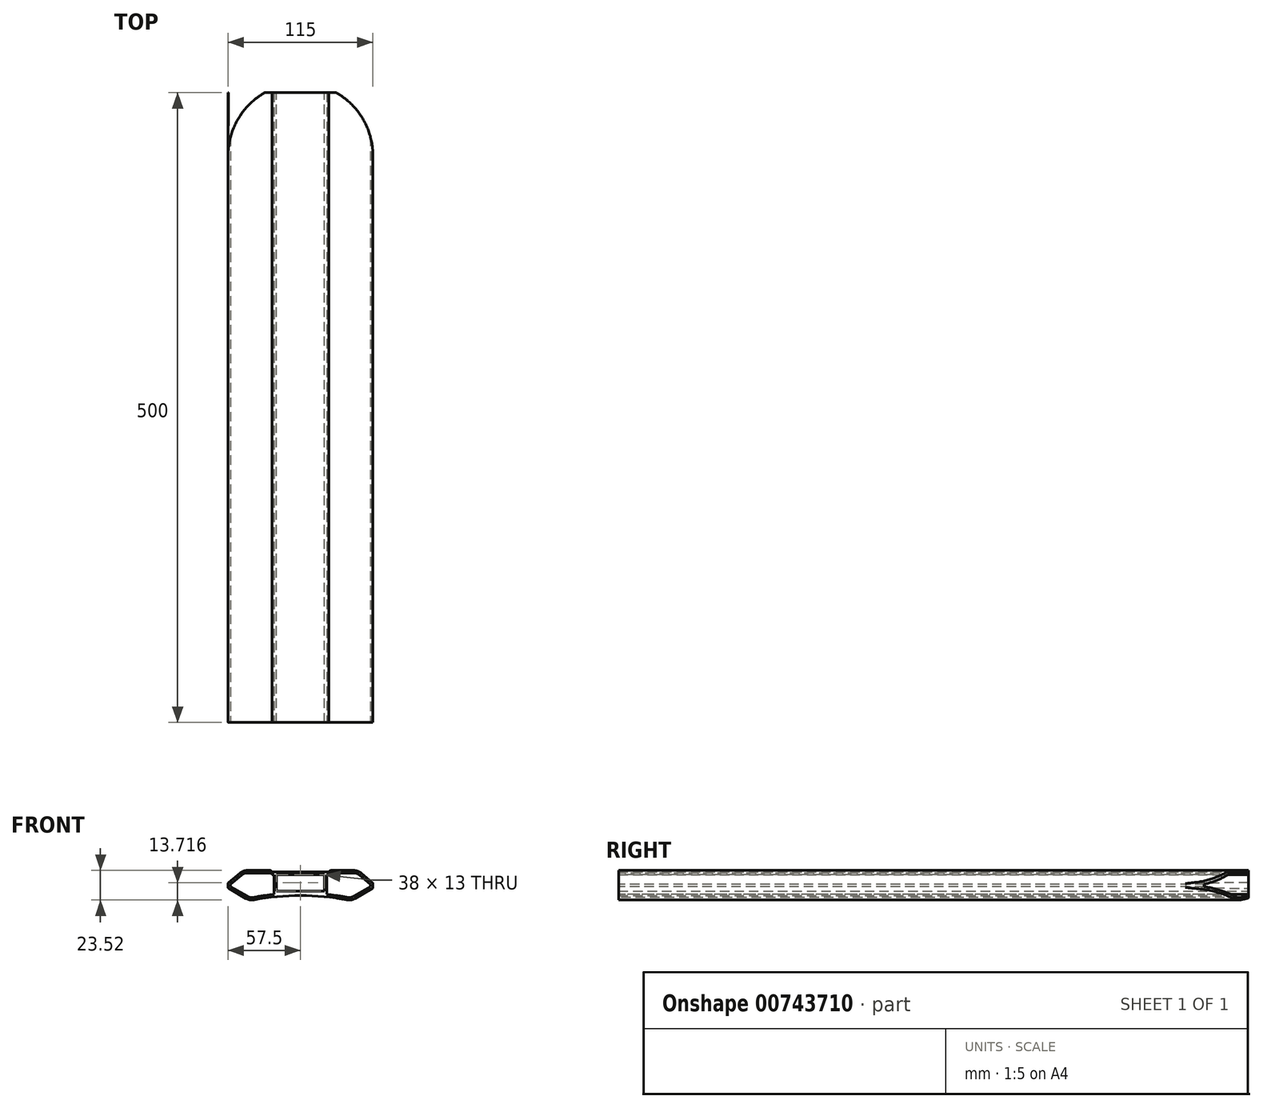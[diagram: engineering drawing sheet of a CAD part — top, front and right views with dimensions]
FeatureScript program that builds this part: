
annotation { "Feature Type Name" : "Feature", "Feature Type Description" : "" }
export const myFeature = defineFeature(function(context is Context, id is Id, definition is map)
    precondition{}
    {
        {
            var Q0;
            Q0=qCreatedBy(makeId("Front.planeOp"),FACE);
            var sketch = newSketch(context, id + "F0", { "sketchPlane" : qUnion([Q0])});
            skLineSegment(sketch, "E0", {"start": v(0, 0) * mm, "end": v(0, 25) * mm, "construction": true});
            skLineSegment(sketch, "E1", {"start": v(0, 5.38) * mm, "end": v(22.5, 5.38) * mm});
            skLineSegment(sketch, "E2", {"start": v(22.5, 5.38) * mm, "end": v(22.5, 6.68) * mm});
            skLineSegment(sketch, "E3", {"start": v(22.5, 6.68) * mm, "end": v(45.58, 6.68) * mm});
            skLineSegment(sketch, "E4", {"start": v(45.58, 6.68) * mm, "end": v(57.5, -3.32) * mm});
            skLineSegment(sketch, "E5", {"start": v(57.5, -3.32) * mm, "end": v(57.5, -7.32) * mm});
            skLineSegment(sketch, "E6", {"start": v(57.5, -7.32) * mm, "end": v(40.18, -17.32) * mm});
            skLineSegment(sketch, "E7.MirrorCS", {"start": v(-45.58, 6.68) * mm, "end": v(-57.5, -3.32) * mm});
            skLineSegment(sketch, "E8.MirrorCS", {"start": v(-22.5, 5.38) * mm, "end": v(-22.5, 6.68) * mm});
            skLineSegment(sketch, "E9.MirrorCS", {"start": v(-57.5, -3.32) * mm, "end": v(-57.5, -7.32) * mm});
            skLineSegment(sketch, "E10.MirrorCS", {"start": v(-22.5, 6.68) * mm, "end": v(-45.58, 6.68) * mm});
            skLineSegment(sketch, "E11.MirrorCS", {"start": v(0, 5.38) * mm, "end": v(-22.5, 5.38) * mm});
            skLineSegment(sketch, "E12.MirrorCS", {"start": v(-57.5, -7.32) * mm, "end": v(-40.18, -17.32) * mm});
            skArc(sketch, "E13", {"start": v(40.18, -17.32) * mm, "mid": v(0, -13.25) * mm, "end": v(-40.18, -17.32) * mm});
            skSolve(sketch);
        }
        {
            var Q0;
            Q0=makeQuery(id+"F0.imprint","IMPRINT",FACE,{"disambiguationData":[TD([[makeQuery(id+"F0.imprint","IMPRINT",EDGE,{"derivedFrom":sQuery(id+"F0.wireOp",EDGE,"E1")}),-1.0]])]});
            var sketch = newSketch(context, id + "F1", { "sketchPlane" : qUnion([Q0])});
            skLineSegment(sketch, "E14.bottom", {"start": v(-19, 3.38) * mm, "end": v(19, 3.38) * mm});
            skLineSegment(sketch, "E14.top", {"start": v(-19, -9.62) * mm, "end": v(19, -9.62) * mm});
            skLineSegment(sketch, "E14.left", {"start": v(-19, 3.38) * mm, "end": v(-19, -9.62) * mm});
            skLineSegment(sketch, "E14.right", {"start": v(19, 3.38) * mm, "end": v(19, -9.62) * mm});
            skLineSegment(sketch, "E15", {"start": v(0, 0) * mm, "end": v(0, -33.5) * mm, "construction": true});
            skSolve(sketch);
        }
        {
            var Q0;
            Q0=makeQuery(id+"F0.imprint","IMPRINT",FACE,{"disambiguationData":[TD([[makeQuery(id+"F0.imprint","IMPRINT",EDGE,{"derivedFrom":sQuery(id+"F0.wireOp",EDGE,"E1")}),-1.0]])]});
            extrude(context, id + "F2", {"entities" : qUnion([Q0]), "depth" : 500 * mm, "offsetDistance" : 25 * mm});
        }
        {
            var Q0;
            Q0=makeQuery(id+"F1.imprint","IMPRINT",FACE,{"disambiguationData":[TD([[makeQuery(id+"F1.imprint","IMPRINT",EDGE,{"derivedFrom":sQuery(id+"F1.wireOp",EDGE,"E14.bottom")}),-1.0]])]});
            extrude(context, id + "F3", {"entities" : qUnion([Q0]), "operationType" : NewBodyOperationType.REMOVE, "depth" : 600 * mm, "offsetDistance" : 25 * mm});
        }
        {
            var Q0;
            Q0=makeQuery(id+"F2.opExtrude","SWEPT_EDGE",EDGE,{"disambiguationData":[OSD([sQuery(id+"F0.wireOp",EDGE,"E8.MirrorCS"),sQuery(id+"F0.wireOp",EDGE,"E10.MirrorCS")])]});
            var Q1;
            Q1=makeQuery(id+"F2.opExtrude","SWEPT_EDGE",EDGE,{"disambiguationData":[OSD([sQuery(id+"F0.wireOp",EDGE,"E2"),sQuery(id+"F0.wireOp",EDGE,"E3")])]});
            fillet(context, id + "F4", {"entities" : qUnion([Q0, Q1]), "radius" : 2 * mm, "tangentPropagation" : true, "allowEdgeOverflow" : false});
        }
        {
            var Q0;
            Q0=makeQuery(id+"F2.opExtrude","SWEPT_EDGE",EDGE,{"disambiguationData":[OSD([sQuery(id+"F0.wireOp",EDGE,"E7.MirrorCS"),sQuery(id+"F0.wireOp",EDGE,"E10.MirrorCS")])]});
            var Q1;
            Q1=makeQuery(id+"F2.opExtrude","SWEPT_EDGE",EDGE,{"disambiguationData":[OSD([sQuery(id+"F0.wireOp",EDGE,"E12.MirrorCS"),sQuery(id+"F0.wireOp",EDGE,"E13")])]});
            var Q2;
            Q2=makeQuery(id+"F2.opExtrude","SWEPT_EDGE",EDGE,{"disambiguationData":[OSD([sQuery(id+"F0.wireOp",EDGE,"E6"),sQuery(id+"F0.wireOp",EDGE,"E13")])]});
            var Q3;
            Q3=makeQuery(id+"F2.opExtrude","SWEPT_EDGE",EDGE,{"disambiguationData":[OSD([sQuery(id+"F0.wireOp",EDGE,"E3"),sQuery(id+"F0.wireOp",EDGE,"E4")])]});
            fillet(context, id + "F5", {"entities" : qUnion([Q0, Q1, Q2, Q3]), "radius" : 9 * mm, "tangentPropagation" : true, "allowEdgeOverflow" : false});
        }
        {
            var Q0;
            Q0=makeQuery(id+"F2.opExtrude","SWEPT_EDGE",EDGE,{"disambiguationData":[OSD([sQuery(id+"F0.wireOp",EDGE,"E4"),sQuery(id+"F0.wireOp",EDGE,"E5")])]});
            var Q1;
            Q1=makeQuery(id+"F2.opExtrude","SWEPT_EDGE",EDGE,{"disambiguationData":[OSD([sQuery(id+"F0.wireOp",EDGE,"E5"),sQuery(id+"F0.wireOp",EDGE,"E6")])]});
            var Q2;
            Q2=makeQuery(id+"F2.opExtrude","SWEPT_EDGE",EDGE,{"disambiguationData":[OSD([sQuery(id+"F0.wireOp",EDGE,"E9.MirrorCS"),sQuery(id+"F0.wireOp",EDGE,"E12.MirrorCS")])]});
            var Q3;
            Q3=makeQuery(id+"F2.opExtrude","SWEPT_EDGE",EDGE,{"disambiguationData":[OSD([sQuery(id+"F0.wireOp",EDGE,"E7.MirrorCS"),sQuery(id+"F0.wireOp",EDGE,"E9.MirrorCS")])]});
            fillet(context, id + "F6", {"entities" : qUnion([Q0, Q1, Q2, Q3]), "radius" : 1 * mm, "tangentPropagation" : true, "allowEdgeOverflow" : false});
        }
        {
            var Q0;
            Q0=makeQuery(id+"F2.opExtrude","CAP_FACE",FACE,{"disambiguationData":[OSD([sQuery(id+"F0.wireOp",EDGE,"E1"),sQuery(id+"F0.wireOp",EDGE,"E2"),sQuery(id+"F0.wireOp",EDGE,"E3"),sQuery(id+"F0.wireOp",EDGE,"E4"),sQuery(id+"F0.wireOp",EDGE,"E5"),sQuery(id+"F0.wireOp",EDGE,"E6"),sQuery(id+"F0.wireOp",EDGE,"E7.MirrorCS"),sQuery(id+"F0.wireOp",EDGE,"E8.MirrorCS"),sQuery(id+"F0.wireOp",EDGE,"E9.MirrorCS"),sQuery(id+"F0.wireOp",EDGE,"E10.MirrorCS"),sQuery(id+"F0.wireOp",EDGE,"E11.MirrorCS"),sQuery(id+"F0.wireOp",EDGE,"E12.MirrorCS"),sQuery(id+"F0.wireOp",EDGE,"E13")])],"isStart":false});
            var sketch = newSketch(context, id + "F7", { "sketchPlane" : qUnion([Q0])});
            skLineSegment(sketch, "E16.0.0", {"start": v(-48.1, 4.57) * mm, "end": v(-57.14, -3.02) * mm});
            skArc(sketch, "E16.0.1", {"start": v(-57.14, -3.02) * mm, "mid": v(-57.4, -3.37) * mm, "end": v(-57.5, -3.8) * mm});
            skLineSegment(sketch, "E16.0.2", {"start": v(-57.5, -3.8) * mm, "end": v(-57.5, -6.75) * mm});
            skArc(sketch, "E16.0.3", {"start": v(-57.5, -6.75) * mm, "mid": v(-57.37, -7.25) * mm, "end": v(-57, -7.61) * mm});
            skLineSegment(sketch, "E16.0.4", {"start": v(-57, -7.61) * mm, "end": v(-43.1, -15.64) * mm});
            skArc(sketch, "E16.0.5", {"start": v(-43.1, -15.64) * mm, "mid": v(-40.12, -16.71) * mm, "end": v(-36.94, -16.69) * mm});
            skArc(sketch, "E16.0.6", {"start": v(-36.94, -16.69) * mm, "mid": v(0, -13.25) * mm, "end": v(36.94, -16.69) * mm});
            skArc(sketch, "E16.0.7", {"start": v(36.94, -16.69) * mm, "mid": v(40.12, -16.71) * mm, "end": v(43.1, -15.64) * mm});
            skLineSegment(sketch, "E16.0.8", {"start": v(43.1, -15.64) * mm, "end": v(57, -7.61) * mm});
            skArc(sketch, "E16.0.9", {"start": v(57, -7.61) * mm, "mid": v(57.37, -7.25) * mm, "end": v(57.5, -6.75) * mm});
            skLineSegment(sketch, "E16.0.10", {"start": v(57.5, -6.75) * mm, "end": v(57.5, -3.8) * mm});
            skArc(sketch, "E16.0.11", {"start": v(57.5, -3.8) * mm, "mid": v(57.4, -3.37) * mm, "end": v(57.14, -3.02) * mm});
            skLineSegment(sketch, "E16.0.12", {"start": v(57.14, -3.02) * mm, "end": v(48.1, 4.57) * mm});
            skArc(sketch, "E16.0.13", {"start": v(48.1, 4.57) * mm, "mid": v(45.38, 6.13) * mm, "end": v(42.3, 6.68) * mm});
            skLineSegment(sketch, "E16.0.14", {"start": v(42.3, 6.68) * mm, "end": v(24.37, 6.68) * mm});
            skArc(sketch, "E16.0.15", {"start": v(24.37, 6.68) * mm, "mid": v(23.23, 6.32) * mm, "end": v(22.5, 5.38) * mm});
            skLineSegment(sketch, "E16.0.16", {"start": v(22.5, 5.38) * mm, "end": v(-22.5, 5.38) * mm});
            skArc(sketch, "E16.0.17", {"start": v(-22.5, 5.38) * mm, "mid": v(-23.23, 6.32) * mm, "end": v(-24.37, 6.68) * mm});
            skLineSegment(sketch, "E16.0.18", {"start": v(-24.37, 6.68) * mm, "end": v(-42.3, 6.68) * mm});
            skArc(sketch, "E16.0.19", {"start": v(-42.3, 6.68) * mm, "mid": v(-45.38, 6.13) * mm, "end": v(-48.1, 4.57) * mm});
            skArc(sketch, "E17.0", {"start": v(-37.3, -14.72) * mm, "mid": v(0, -11.25) * mm, "end": v(37.3, -14.72) * mm});
            skArc(sketch, "E17.1", {"start": v(-42.1, -13.9) * mm, "mid": v(-39.78, -14.74) * mm, "end": v(-37.3, -14.72) * mm});
            skLineSegment(sketch, "E17.2", {"start": v(-55.5, -6.17) * mm, "end": v(-42.1, -13.9) * mm});
            skLineSegment(sketch, "E17.3", {"start": v(-24.37, 4.68) * mm, "end": v(-42.3, 4.68) * mm});
            skArc(sketch, "E17.4", {"start": v(-42.3, 4.68) * mm, "mid": v(-44.7, 4.25) * mm, "end": v(-46.8, 3.04) * mm});
            skLineSegment(sketch, "E17.5", {"start": v(-46.8, 3.04) * mm, "end": v(-55.5, -4.26) * mm});
            skLineSegment(sketch, "E17.6", {"start": v(-55.5, -4.26) * mm, "end": v(-55.5, -6.17) * mm});
            skLineSegment(sketch, "E18.0", {"start": v(-21, 3.38) * mm, "end": v(-21, -12.34) * mm});
            skLineSegment(sketch, "E19.0", {"start": v(22.5, 3.38) * mm, "end": v(-22.5, 3.38) * mm});
            skArc(sketch, "E20", {"start": v(-24.37, 4.68) * mm, "mid": v(-23.23, 4.32) * mm, "end": v(-22.5, 3.38) * mm});
            skLineSegment(sketch, "E21.0", {"start": v(42.3, 4.68) * mm, "end": v(24.37, 4.68) * mm});
            skArc(sketch, "E21.1", {"start": v(46.8, 3.04) * mm, "mid": v(44.7, 4.25) * mm, "end": v(42.3, 4.68) * mm});
            skArc(sketch, "E21.2", {"start": v(37.3, -14.72) * mm, "mid": v(39.78, -14.74) * mm, "end": v(42.1, -13.9) * mm});
            skLineSegment(sketch, "E21.3", {"start": v(42.1, -13.9) * mm, "end": v(55.5, -6.17) * mm});
            skLineSegment(sketch, "E21.4", {"start": v(55.5, -6.17) * mm, "end": v(55.5, -4.26) * mm});
            skLineSegment(sketch, "E21.5", {"start": v(55.5, -4.26) * mm, "end": v(46.8, 3.04) * mm});
            skLineSegment(sketch, "E22.0", {"start": v(21, 3.38) * mm, "end": v(21, -12.34) * mm});
            skArc(sketch, "E23", {"start": v(24.37, 4.68) * mm, "mid": v(23.23, 4.32) * mm, "end": v(22.5, 3.38) * mm});
            skSolve(sketch);
        }
        {
            var Q0;
            {var subQ1=sQuery(id+"F7.wireOp",EDGE,"E17.1");Q0=makeQuery(id+"F7.imprint","IMPRINT",FACE,{"disambiguationData":[TD([[makeQuery(id+"F7.imprint","IMPRINT",EDGE,{"derivedFrom":subQ1}),1.0]])]});}
            var Q1;
            Q1=makeQuery(id+"F7.imprint","IMPRINT",FACE,{"disambiguationData":[TD([[makeQuery(id+"F7.imprint","IMPRINT",EDGE,{"derivedFrom":sQuery(id+"F7.wireOp",EDGE,"E21.0")}),1.0]])]});
            extrude(context, id + "F8", {"entities" : qUnion([Q0, Q1]), "operationType" : NewBodyOperationType.REMOVE, "endBound" : BoundingType.THROUGH_ALL, "oppositeDirection" : true, "depth" : 25 * mm, "offsetDistance" : 25 * mm});
        }
        {
            var Q0;
            Q0=qCreatedBy(makeId("Top.planeOp"),FACE);
            var sketch = newSketch(context, id + "F9", { "sketchPlane" : qUnion([Q0])});
            skArc(sketch, "E24", {"start": v(57.5, -50) * mm, "mid": v(0, 7.5) * mm, "end": v(-57.5, -50) * mm});
            skLineSegment(sketch, "E25", {"start": v(57.82, 0) * mm, "end": v(57.82, 30) * mm});
            skLineSegment(sketch, "E26", {"start": v(57.82, 30) * mm, "end": v(-57.18, 30) * mm});
            skLineSegment(sketch, "E27", {"start": v(-57.18, 30) * mm, "end": v(-57.18, 0) * mm});
            skLineSegment(sketch, "E28", {"start": v(0, -50) * mm, "end": v(57.5, -50) * mm});
            skLineSegment(sketch, "E29", {"start": v(57.5, -50) * mm, "end": v(57.82, 0) * mm});
            skLineSegment(sketch, "E30", {"start": v(0, -50) * mm, "end": v(-57.5, -50) * mm});
            skLineSegment(sketch, "E31", {"start": v(-57.5, -50) * mm, "end": v(-57.18, 0) * mm});
            skSolve(sketch);
        }
        {
            var Q0;
            Q0=makeQuery(id+"F9.imprint","IMPRINT",FACE,{"disambiguationData":[TD([[makeQuery(id+"F9.imprint","IMPRINT",EDGE,{"derivedFrom":sQuery(id+"F9.wireOp",EDGE,"E25")}),1.0]])]});
            extrude(context, id + "F10", {"entities" : qUnion([Q0]), "operationType" : NewBodyOperationType.REMOVE, "endBound" : BoundingType.THROUGH_ALL, "oppositeDirection" : true, "depth" : 25 * mm, "offsetDistance" : 25 * mm, "hasSecondDirection" : true, "secondDirectionOppositeDirection" : false, "secondDirectionDepth" : 25 * mm});
        }
    });
